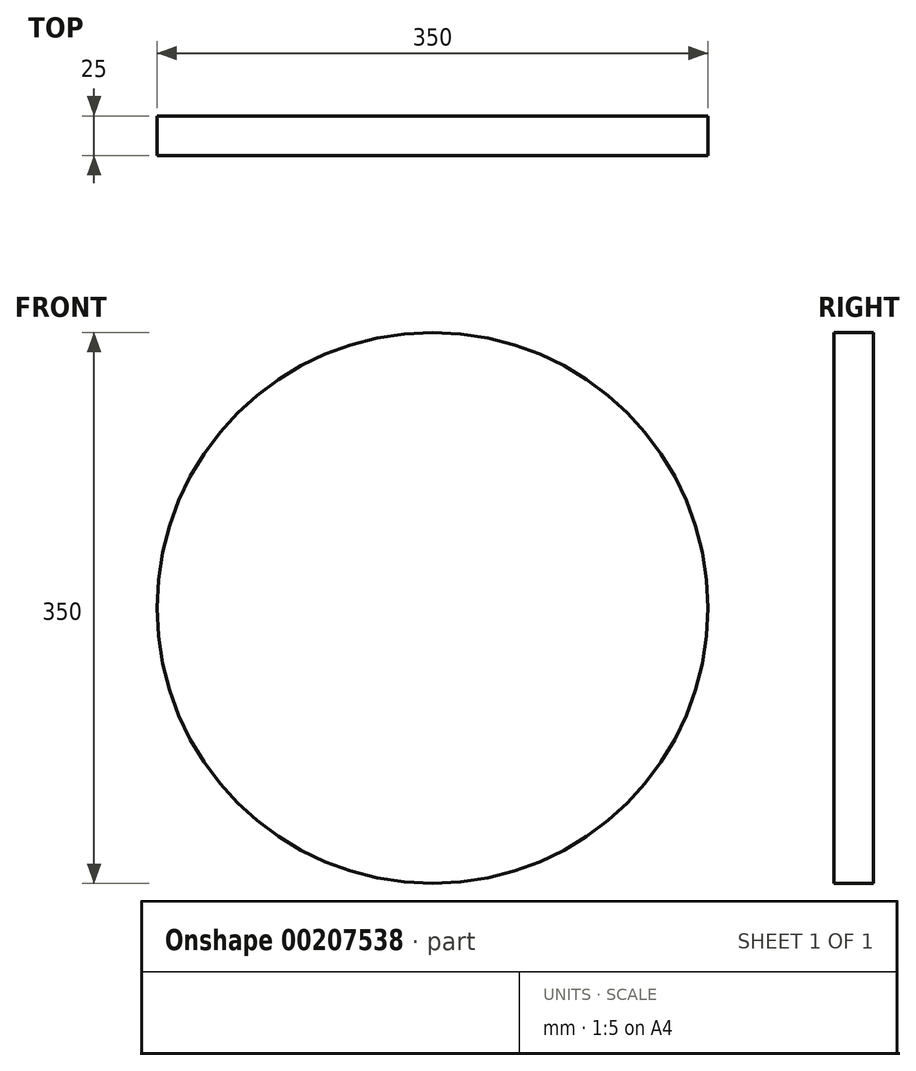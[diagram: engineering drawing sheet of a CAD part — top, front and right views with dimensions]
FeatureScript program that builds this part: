
annotation { "Feature Type Name" : "Feature", "Feature Type Description" : "" }
export const myFeature = defineFeature(function(context is Context, id is Id, definition is map)
    precondition{}
    {
        {
            var Q0;
            Q0=qCreatedBy(makeId("Front.planeOp"),FACE);
            var sketch = newSketch(context, id + "F0", { "sketchPlane" : qUnion([Q0])});
            skCircle(sketch, "E0", {"center": v(0, 0) * mm, "radius": 175 * mm});
            skSolve(sketch);
        }
        {
            var Q0;
            Q0 = qSketchRegion(id + "F0", true);
            extrude(context, id + "F1", {"entities" : qUnion([Q0]), "depth" : 25 * mm});
        }
    });
